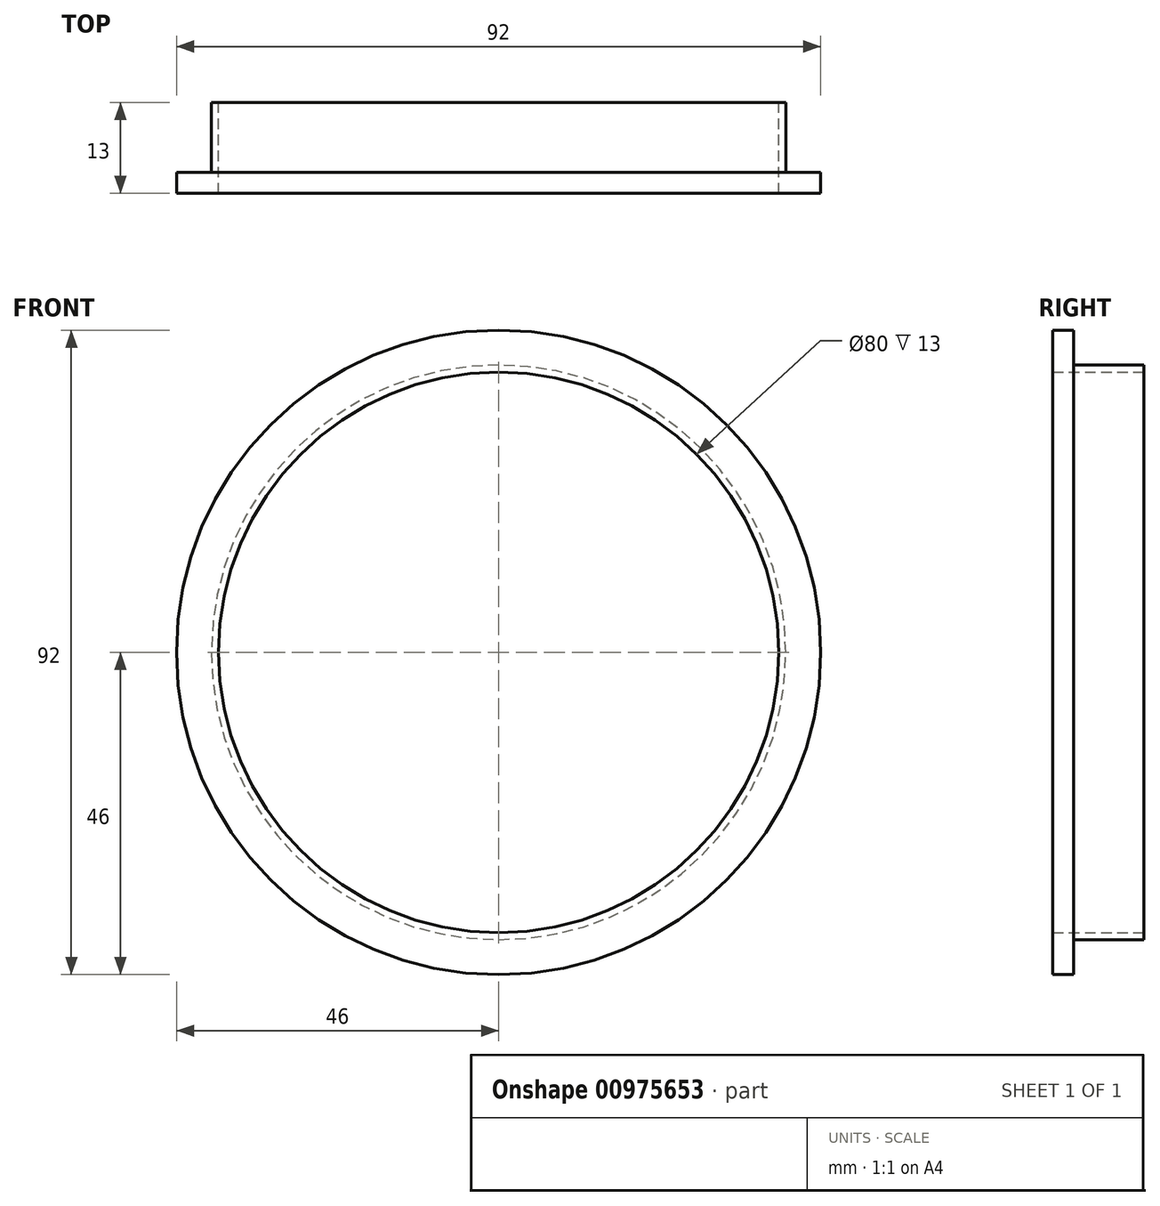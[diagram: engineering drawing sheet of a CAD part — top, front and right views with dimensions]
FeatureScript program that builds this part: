
annotation { "Feature Type Name" : "Feature", "Feature Type Description" : "" }
export const myFeature = defineFeature(function(context is Context, id is Id, definition is map)
    precondition{}
    {
        {
            var Q0;
            Q0=qCreatedBy(makeId("Front.planeOp"),FACE);
            var sketch = newSketch(context, id + "F0", { "sketchPlane" : qUnion([Q0])});
            skCircle(sketch, "E0", {"center": v(0, 0) * mm, "radius": 40 * mm});
            skCircle(sketch, "E1.0", {"center": v(0, 0) * mm, "radius": 41 * mm});
            skSolve(sketch);
        }
        {
            var Q0;
            Q0 = qSketchRegion(id + "F0", true);
            extrude(context, id + "F1", {"entities" : qUnion([Q0]), "depth" : 10 * mm, "offsetDistance" : 25 * mm});
        }
        {
            var Q0;
            Q0=makeQuery(id+"F1.opExtrude","CAP_FACE",FACE,{"disambiguationData":[OSD([sQuery(id+"F0.wireOp",EDGE,"E0"),sQuery(id+"F0.wireOp",EDGE,"E1.0")])],"isStart":false});
            cPlane(context, id + "F2", {"entities" : qUnion([Q0]), "cplaneType" : CPlaneType.OFFSET, "offset" : 0 * mm, "width" : 150 * mm, "height" : 150 * mm});
        }
        {
            var Q0;
            Q0=qCreatedBy(id+"F2.planeOp",FACE);
            var sketch = newSketch(context, id + "F3", { "sketchPlane" : qUnion([Q0])});
            skCircle(sketch, "E2.0", {"center": v(0, 0) * mm, "radius": 40 * mm});
            skCircle(sketch, "E3.0", {"center": v(0, 0) * mm, "radius": 46 * mm});
            skSolve(sketch);
        }
        {
            var Q0;
            Q0 = qSketchRegion(id + "F3", true);
            extrude(context, id + "F4", {"entities" : qUnion([Q0]), "operationType" : NewBodyOperationType.ADD, "depth" : 3 * mm, "offsetDistance" : 25 * mm});
        }
    });
